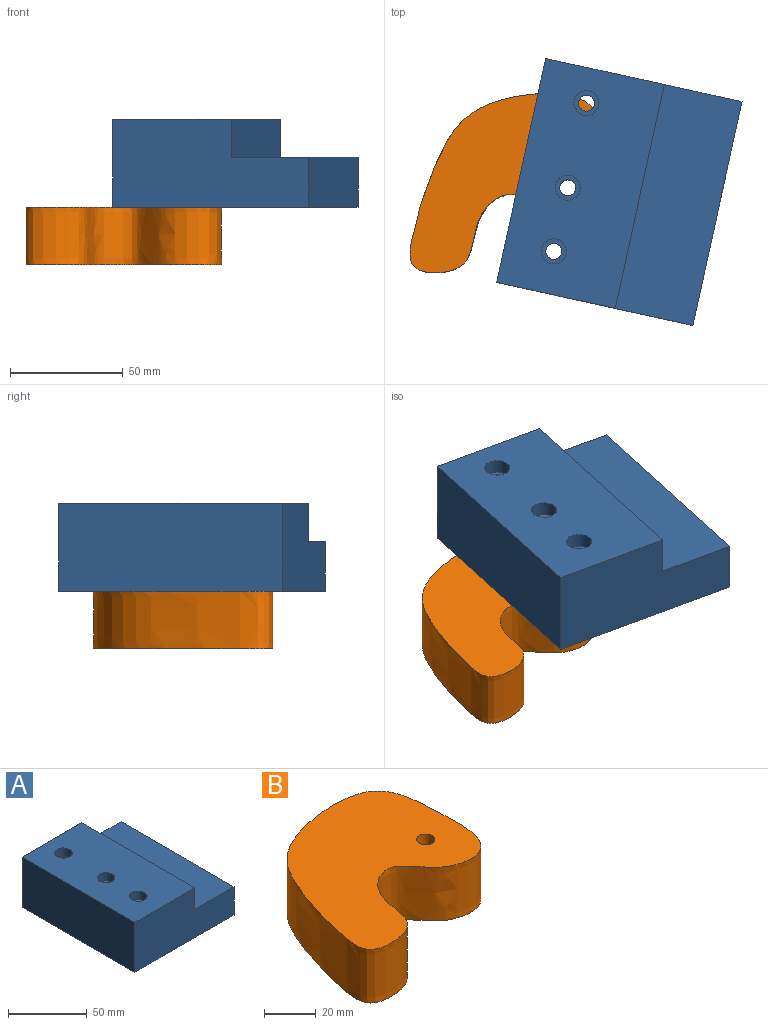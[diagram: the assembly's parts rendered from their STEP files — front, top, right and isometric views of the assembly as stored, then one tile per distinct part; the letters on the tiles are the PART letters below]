
ASSEMBLY  parts=2 mates=1
PART A: 17 faces, bbox 89.1x101.6x39 mm
  f0: plane 101.6x22.09mm, normal (1,0,0), area 2244.1mm2, adj f1,f5,f6,f7
  f1: plane 101.6x35.27mm, normal (0,0,1), area 3582.9mm2, adj f0,f2,f6,f7
  f2: plane 101.6x16.87mm, normal (1,0,0), area 1714.4mm2, adj f1,f3,f6,f7
  f3: plane 101.6x53.85mm, normal (0,0,1), area 5179.8mm2, adj f2,f4,f6,f7,f10,f13,f16
  f4: plane 101.6x38.96mm, normal (-1,0,0), area 3958.6mm2, adj f3,f5,f6,f7
  f5: plane 101.6x89.11mm, normal (0,0,-1), area 8933.6mm2, adj f0,f4,f6,f7,f8,f11,f14
  f6: plane 89.11x38.96mm, normal (0,-1,0), area 2876.9mm2, adj f0,f1,f2,f3,f4,f5
  f7: plane 89.11x38.96mm, normal (0,1,0), area 2876.9mm2, adj f0,f1,f2,f3,f4,f5
  f8: cylinder r=3.57mm len=32.61mm, axis (0,0,1), area 731.3mm2, adj f5,f9
  f9: plane 11.11x11.11mm, normal (0,0,1), area 57mm2, adj f8,f10
  f10: cylinder r=5.56mm len=11.11mm, axis (0,0,1), area 221.7mm2, adj f3,f9
  f11: cylinder r=3.57mm len=32.61mm, axis (0,0,1), area 731.3mm2, adj f5,f12
  f12: plane 11.11x11.11mm, normal (0,0,1), area 57mm2, adj f11,f13
  f13: cylinder r=5.56mm len=11.11mm, axis (0,0,1), area 221.7mm2, adj f3,f12
  f14: cylinder r=3.57mm len=32.61mm, axis (0,0,1), area 731.3mm2, adj f5,f15
  f15: plane 11.11x11.11mm, normal (0,0,1), area 57mm2, adj f14,f16
  f16: cylinder r=5.56mm len=11.11mm, axis (0,0,1), area 221.7mm2, adj f3,f15
PART B: 4 faces, bbox 87.6x83.6x25.4 mm
  f0: extruded ~85.58x81.08mm, area 7529mm2, adj f1,f2
  f1: plane 87.63x83.62mm, normal (0,0,1), area 4329.8mm2, adj f0,f3
  f2: plane 87.63x83.62mm, normal (0,0,-1), area 4329.8mm2, adj f0,f3
  f3: cylinder r=3.57mm len=25.4mm, axis (0,0,1), area 569.5mm2, adj f1,f2
PLACE A rot(axis=(0,0,-1),12.4deg) t=(24.64,-9.17,26.46)mm fixed
PLACE B rot(axis=(0,0,-1),1.8deg) t=(-25.84,-1.28,1.06)mm
MATE revolute A.f11 <-> B.f3  axis (0,0,-1) through (0.06,-6.94,26.46)mm
